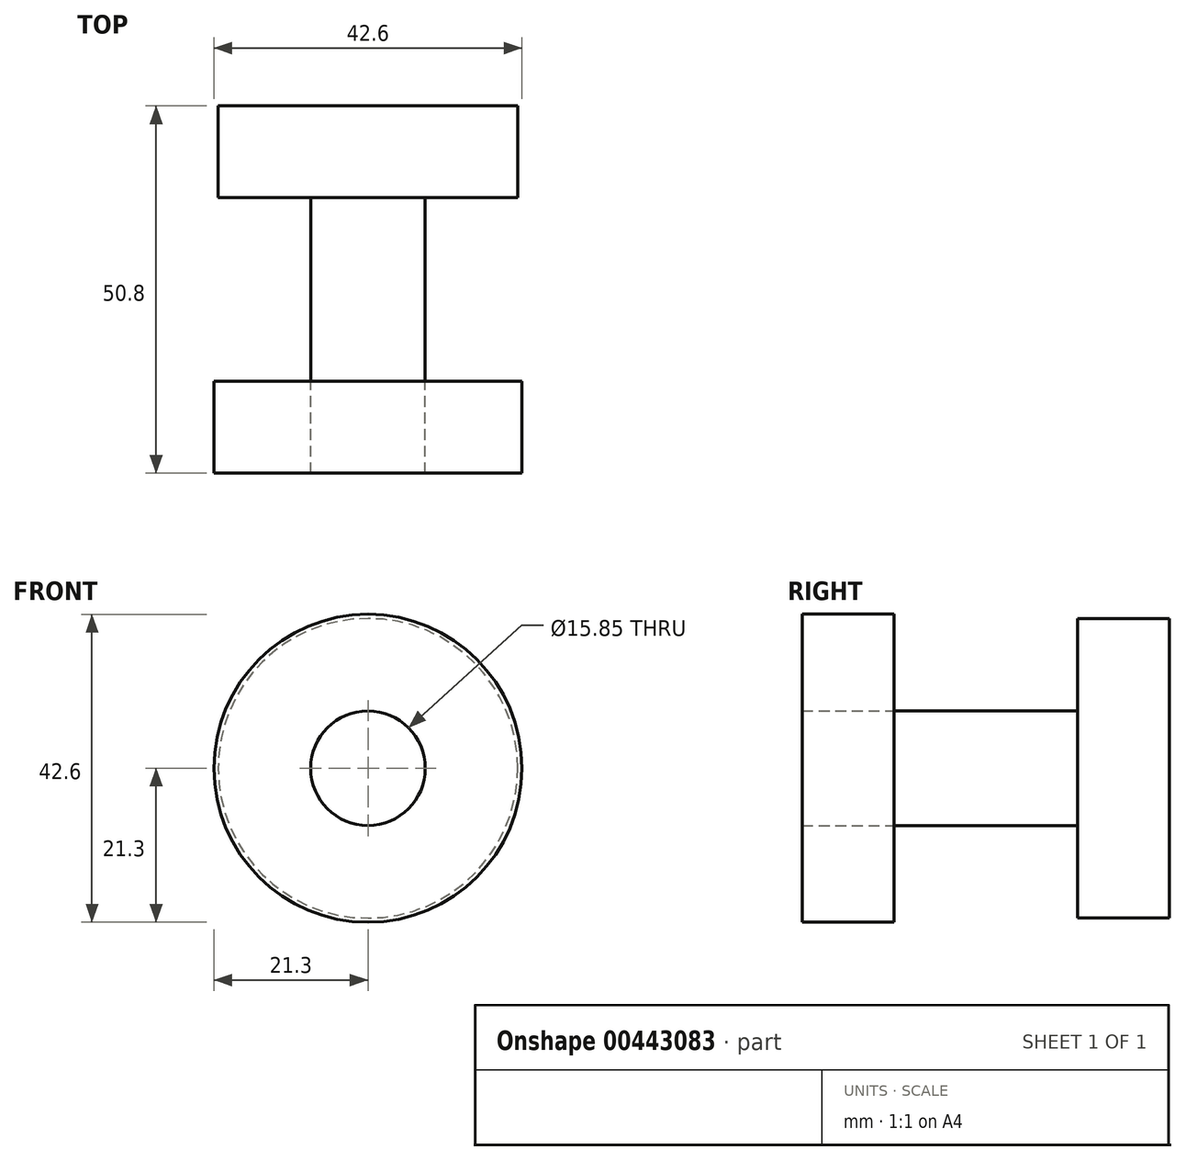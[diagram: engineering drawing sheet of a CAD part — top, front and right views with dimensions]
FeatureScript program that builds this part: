
annotation { "Feature Type Name" : "Feature", "Feature Type Description" : "" }
export const myFeature = defineFeature(function(context is Context, id is Id, definition is map)
    precondition{}
    {
        {
            var Q0;
            Q0=qCreatedBy(makeId("Front.planeOp"),FACE);
            var sketch = newSketch(context, id + "F0", { "sketchPlane" : qUnion([Q0])});
            skCircle(sketch, "E0", {"center": v(0, 0) * mm, "radius": 20.72 * mm});
            skSolve(sketch);
        }
        {
            var Q0;
            Q0=makeQuery(id+"F0.imprint","IMPRINT",FACE,{"disambiguationData":[TD([[makeQuery(id+"F0.imprint","IMPRINT",EDGE,{"derivedFrom":sQuery(id+"F0.wireOp",EDGE,"E0")}),1.0]])]});
            extrude(context, id + "F1", {"entities" : qUnion([Q0]), "depth" : 12.7 * mm});
        }
        {
            var Q0;
            Q0=makeQuery(id+"F1.opExtrude","CAP_FACE",FACE,{"disambiguationData":[OSD([sQuery(id+"F0.wireOp",EDGE,"E0")])],"isStart":false});
            var sketch = newSketch(context, id + "F2", { "sketchPlane" : qUnion([Q0])});
            skCircle(sketch, "E1", {"center": v(0, 0) * mm, "radius": 7.93 * mm});
            skSolve(sketch);
        }
        {
            var Q0;
            Q0=makeQuery(id+"F2.imprint","IMPRINT",FACE,{"disambiguationData":[TD([[makeQuery(id+"F2.imprint","IMPRINT",EDGE,{"derivedFrom":sQuery(id+"F2.wireOp",EDGE,"E1")}),1.0]])]});
            extrude(context, id + "F3", {"entities" : qUnion([Q0]), "operationType" : NewBodyOperationType.ADD, "depth" : 25.4 * mm});
        }
        {
            var Q0;
            Q0=makeQuery(id+"F3.opExtrude","CAP_FACE",FACE,{"disambiguationData":[OSD([sQuery(id+"F2.wireOp",EDGE,"E1")])],"isStart":false});
            var sketch = newSketch(context, id + "F4", { "sketchPlane" : qUnion([Q0])});
            skCircle(sketch, "E2", {"center": v(0, 0) * mm, "radius": 21.3 * mm});
            skSolve(sketch);
        }
        {
            var Q0;
            Q0=makeQuery(id+"F4.imprint","IMPRINT",FACE,{"disambiguationData":[TD([[makeQuery(id+"F4.imprint","IMPRINT",EDGE,{"derivedFrom":sQuery(id+"F4.wireOp",EDGE,"E2")}),1.0]])]});
            extrude(context, id + "F5", {"entities" : qUnion([Q0]), "depth" : 12.7 * mm});
        }
        {
            var Q0;
            Q0=makeQuery(id+"F3.opExtrude","CAP_FACE",FACE,{"disambiguationData":[OSD([sQuery(id+"F2.wireOp",EDGE,"E1")])],"isStart":false});
            extrude(context, id + "F6", {"entities" : qUnion([Q0]), "depth" : 12.7 * mm});
        }
    });
